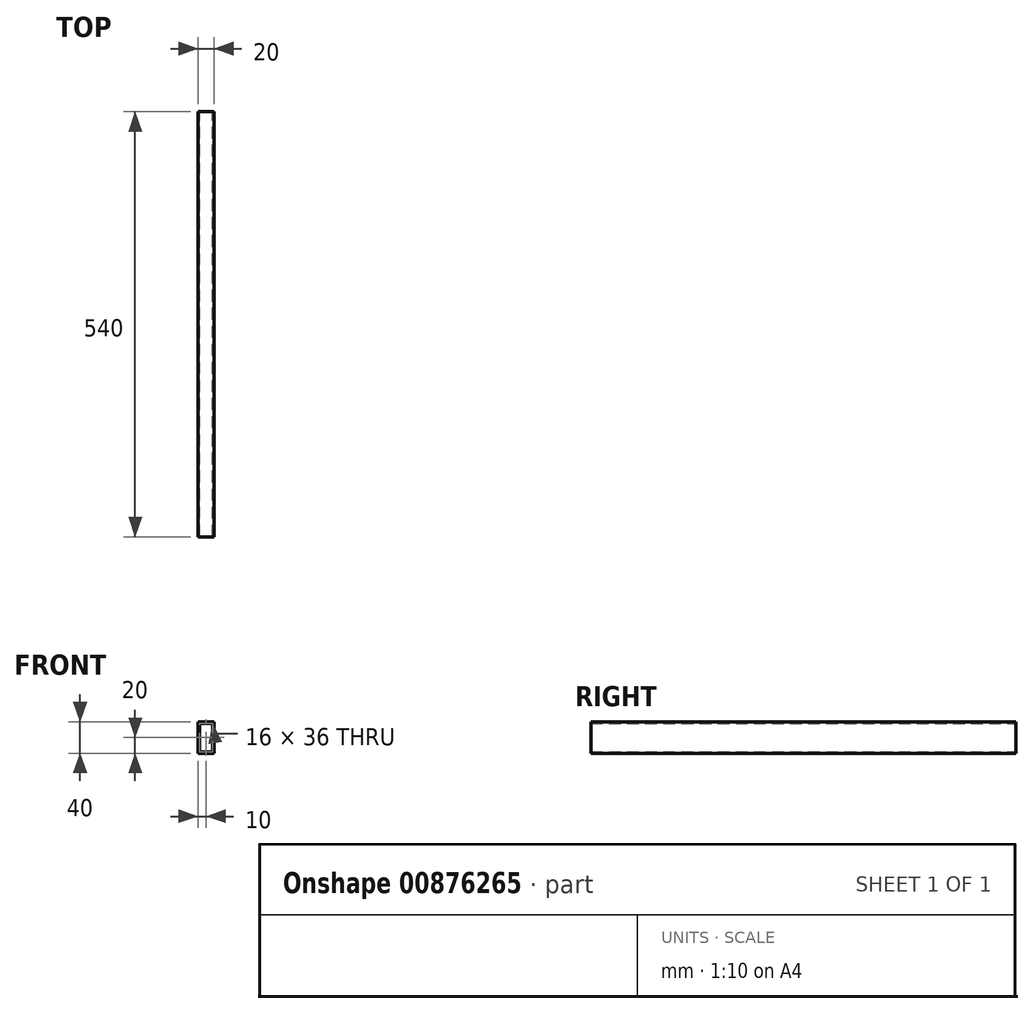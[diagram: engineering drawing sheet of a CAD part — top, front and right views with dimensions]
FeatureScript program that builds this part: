
annotation { "Feature Type Name" : "Feature", "Feature Type Description" : "" }
export const myFeature = defineFeature(function(context is Context, id is Id, definition is map)
    precondition{}
    {
        {
            var Q0;
            Q0=qCreatedBy(makeId("Front.planeOp"),FACE);
            var sketch = newSketch(context, id + "F0", { "sketchPlane" : qUnion([Q0])});
            skLineSegment(sketch, "E0.bottom", {"start": v(0, 0) * mm, "end": v(20, 0) * mm});
            skLineSegment(sketch, "E0.top", {"start": v(0, -40) * mm, "end": v(20, -40) * mm});
            skLineSegment(sketch, "E0.left", {"start": v(0, 0) * mm, "end": v(0, -40) * mm});
            skLineSegment(sketch, "E0.right", {"start": v(20, 0) * mm, "end": v(20, -40) * mm});
            skLineSegment(sketch, "E1.0", {"start": v(2, -2) * mm, "end": v(18, -2) * mm});
            skLineSegment(sketch, "E1.1", {"start": v(2, -2) * mm, "end": v(2, -38) * mm});
            skLineSegment(sketch, "E1.2", {"start": v(2, -38) * mm, "end": v(18, -38) * mm});
            skLineSegment(sketch, "E1.3", {"start": v(18, -2) * mm, "end": v(18, -38) * mm});
            skSolve(sketch);
        }
        {
            var Q0;
            Q0=makeQuery(id+"F0.imprint","IMPRINT",FACE,{"disambiguationData":[TD([[makeQuery(id+"F0.imprint","IMPRINT",EDGE,{"derivedFrom":sQuery(id+"F0.wireOp",EDGE,"E0.bottom")}),-1.0]])]});
            extrude(context, id + "F1", {"entities" : qUnion([Q0]), "depth" : 540 * mm, "offsetDistance" : 25.4 * mm});
        }
    });
